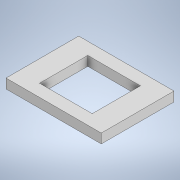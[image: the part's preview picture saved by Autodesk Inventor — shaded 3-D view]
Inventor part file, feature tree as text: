
AUTODESK INVENTOR PART (.ipt)
format: ipt  version: 2020 (Build 240168000, 168)  size: 105,984 bytes
history: native  units: in
note: dims shown in document units (in); Inventor stores cm internally (conversion verified against a paired STEP export)
features: extrude x2, sketch x2
ambient origin geometry x8: Origin, YZ Plane, XZ Plane, XY Plane, X Axis, Y Axis, Z Axis, Center Point
bodies: Solid1 (feature_tree)
feature tree (4):
  extrude  "Extrusion1"  Depth=0.961in
  extrude  "Extrusion2"  Depth=0.6964in
  sketch  "Sketch1"  dims[d0=1.259in d1=0.961in]
  sketch  "Sketch2"  dims[d2=0.125in d3=0.0in d4=0.6964in d5=0.6374in d6=1.0in d7=0.0in]
